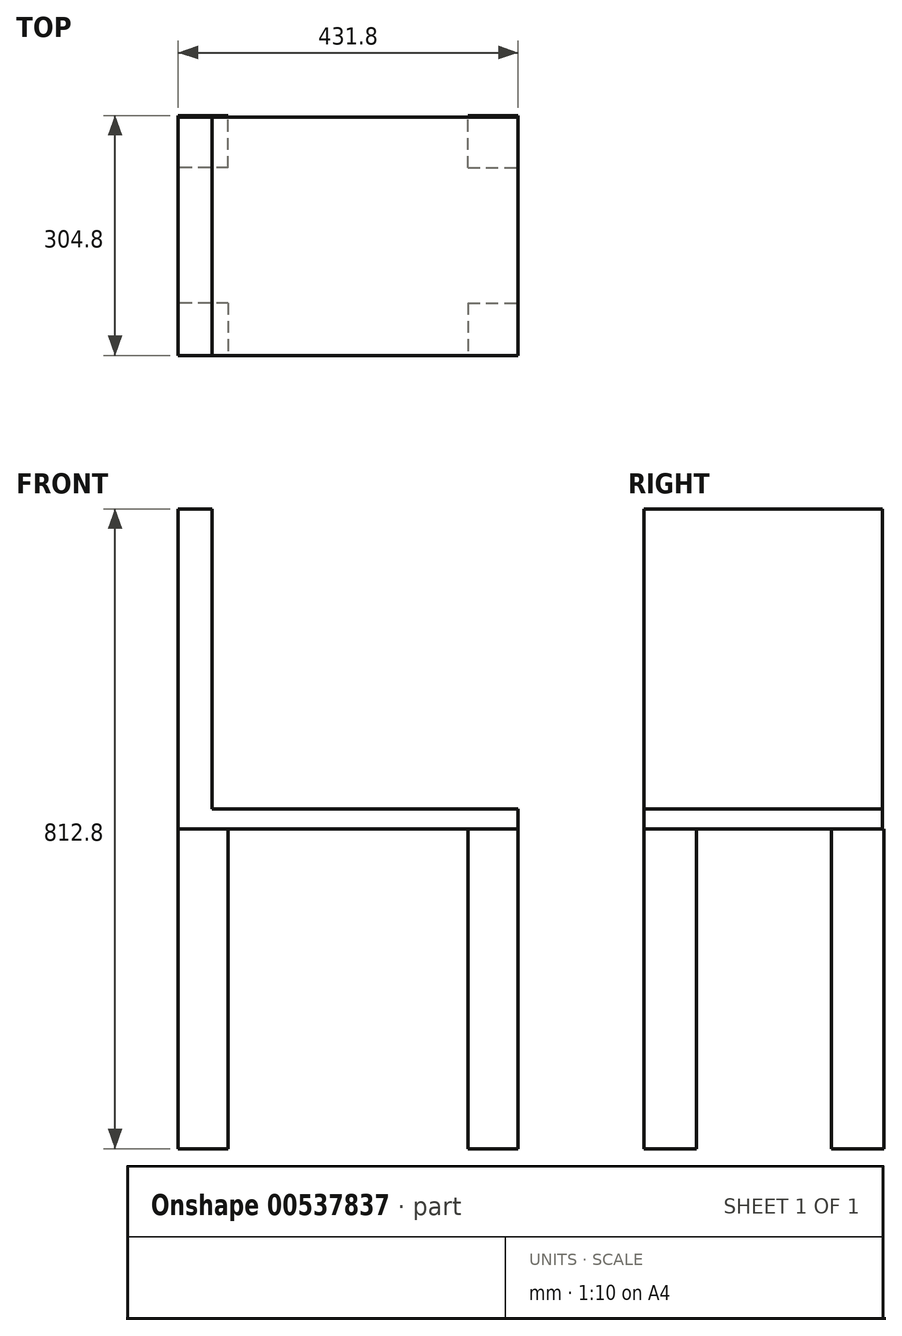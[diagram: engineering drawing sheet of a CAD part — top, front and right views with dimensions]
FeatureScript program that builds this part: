
annotation { "Feature Type Name" : "Feature", "Feature Type Description" : "" }
export const myFeature = defineFeature(function(context is Context, id is Id, definition is map)
    precondition{}
    {
        {
            var Q0;
            Q0=qCreatedBy(makeId("Top.planeOp"),FACE);
            var sketch = newSketch(context, id + "F0", { "sketchPlane" : qUnion([Q0])});
            skLineSegment(sketch, "E0", {"start": v(0, 0) * mm, "end": v(0, 66.6) * mm});
            skLineSegment(sketch, "E1", {"start": v(63.5, 66.6) * mm, "end": v(63.5, 0) * mm});
            skLineSegment(sketch, "E2", {"start": v(63.5, 0) * mm, "end": v(0, 0) * mm});
            skLineSegment(sketch, "E3", {"start": v(63.5, 66.6) * mm, "end": v(0, 66.6) * mm});
            skLineSegment(sketch, "E4", {"start": v(63.5, 0) * mm, "end": v(368.3, 0) * mm});
            skLineSegment(sketch, "E5", {"start": v(215.9, 0) * mm, "end": v(215.9, 304.8) * mm});
            skLineSegment(sketch, "E6.MirrorCS", {"start": v(368.3, 66.6) * mm, "end": v(431.8, 66.6) * mm});
            skLineSegment(sketch, "E7.MirrorCS", {"start": v(431.8, 0) * mm, "end": v(431.8, 66.6) * mm});
            skLineSegment(sketch, "E8.MirrorCS", {"start": v(368.3, 0) * mm, "end": v(431.8, 0) * mm});
            skLineSegment(sketch, "E9.MirrorCS", {"start": v(368.3, 66.6) * mm, "end": v(368.3, 0) * mm});
            skLineSegment(sketch, "E10.MirrorCS", {"start": v(368.3, 0) * mm, "end": v(63.5, 0) * mm});
            skLineSegment(sketch, "E11", {"start": v(215.9, 152.4) * mm, "end": v(122.76, 152.4) * mm});
            skLineSegment(sketch, "E12.MirrorCS", {"start": v(63.5, 238.2) * mm, "end": v(0, 238.2) * mm});
            skLineSegment(sketch, "E13.MirrorCS", {"start": v(63.5, 238.2) * mm, "end": v(63.5, 304.8) * mm});
            skLineSegment(sketch, "E14.MirrorCS", {"start": v(63.5, 304.8) * mm, "end": v(0, 304.8) * mm});
            skLineSegment(sketch, "E15.MirrorCS", {"start": v(0, 304.8) * mm, "end": v(0, 238.2) * mm});
            skLineSegment(sketch, "E16.MirrorCS", {"start": v(368.3, 238.2) * mm, "end": v(431.8, 238.2) * mm});
            skLineSegment(sketch, "E17.MirrorCS", {"start": v(368.3, 238.2) * mm, "end": v(368.3, 304.8) * mm});
            skLineSegment(sketch, "E18.MirrorCS", {"start": v(368.3, 304.8) * mm, "end": v(431.8, 304.8) * mm});
            skLineSegment(sketch, "E19.MirrorCS", {"start": v(431.8, 304.8) * mm, "end": v(431.8, 238.2) * mm});
            skSolve(sketch);
        }
        {
            var Q0;
            Q0 = qSketchRegion(id + "F0", true);
            extrude(context, id + "F1", {"entities" : qUnion([Q0]), "depth" : 406.4 * mm, "offsetDistance" : 25.4 * mm});
        }
        {
            var Q0;
            Q0=makeQuery(id+"F1.opExtrude","CAP_FACE",FACE,{"disambiguationData":[OSD([sQuery(id+"F0.wireOp",EDGE,"E6.MirrorCS"),sQuery(id+"F0.wireOp",EDGE,"E7.MirrorCS"),sQuery(id+"F0.wireOp",EDGE,"E8.MirrorCS"),sQuery(id+"F0.wireOp",EDGE,"E9.MirrorCS")])],"isStart":false});
            var sketch = newSketch(context, id + "F2", { "sketchPlane" : qUnion([Q0])});
            skLineSegment(sketch, "E20", {"start": v(431.8, 0) * mm, "end": v(0, 0) * mm});
            skLineSegment(sketch, "E21", {"start": v(0, 0) * mm, "end": v(0, 302.62) * mm});
            skLineSegment(sketch, "E22", {"start": v(0, 302.62) * mm, "end": v(431.8, 302.62) * mm});
            skLineSegment(sketch, "E23", {"start": v(431.8, 302.62) * mm, "end": v(431.8, 0) * mm});
            skSolve(sketch);
        }
        {
            var Q0;
            Q0 = qSketchRegion(id + "F2", true);
            extrude(context, id + "F3", {"entities" : qUnion([Q0]), "depth" : 25.4 * mm, "offsetDistance" : 25.4 * mm});
        }
        {
            var Q0;
            Q0=makeQuery(id+"F3.opExtrude","CAP_FACE",FACE,{"disambiguationData":[OSD([sQuery(id+"F2.wireOp",EDGE,"E20"),sQuery(id+"F2.wireOp",EDGE,"E21"),sQuery(id+"F2.wireOp",EDGE,"E22"),sQuery(id+"F2.wireOp",EDGE,"E23")])],"isStart":false});
            var sketch = newSketch(context, id + "F4", { "sketchPlane" : qUnion([Q0])});
            skLineSegment(sketch, "E24", {"start": v(0, 0) * mm, "end": v(0, 302.62) * mm});
            skLineSegment(sketch, "E25", {"start": v(0, 302.62) * mm, "end": v(43.12, 302.62) * mm});
            skLineSegment(sketch, "E26", {"start": v(43.12, 302.62) * mm, "end": v(43.12, 0) * mm});
            skLineSegment(sketch, "E27", {"start": v(43.12, 0) * mm, "end": v(0, 0) * mm});
            skSolve(sketch);
        }
        {
            var Q0;
            Q0 = qSketchRegion(id + "F4", true);
            extrude(context, id + "F5", {"entities" : qUnion([Q0]), "operationType" : NewBodyOperationType.ADD, "depth" : 381 * mm, "offsetDistance" : 25.4 * mm});
        }
    });
